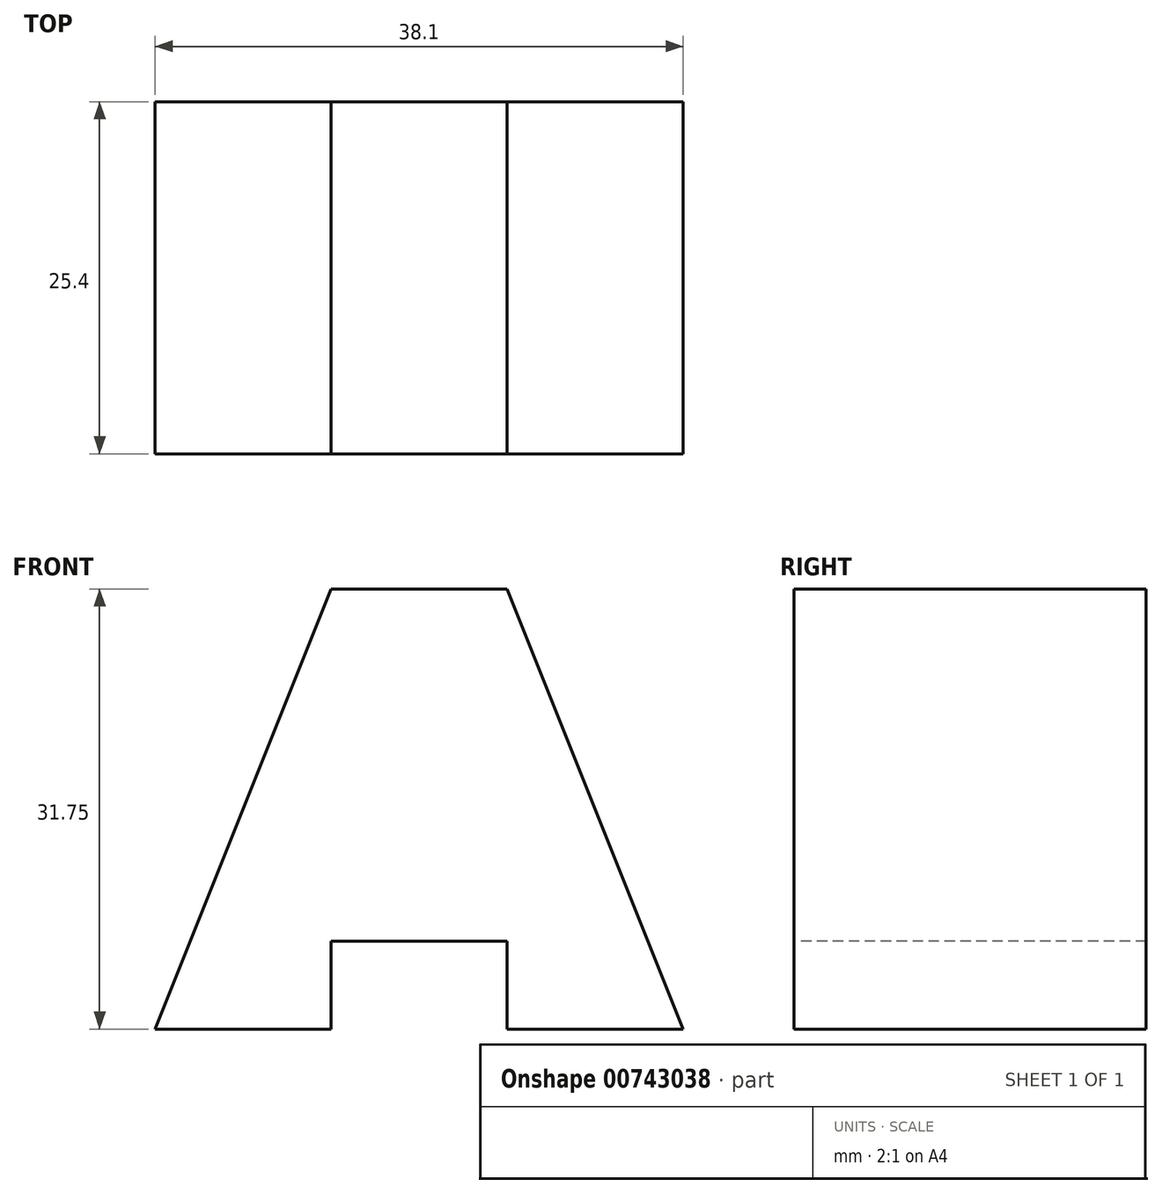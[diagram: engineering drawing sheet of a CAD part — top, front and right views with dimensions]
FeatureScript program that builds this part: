
annotation { "Feature Type Name" : "Feature", "Feature Type Description" : "" }
export const myFeature = defineFeature(function(context is Context, id is Id, definition is map)
    precondition{}
    {
        {
            var Q0;
            Q0=qCreatedBy(makeId("Front.planeOp"),FACE);
            var sketch = newSketch(context, id + "F0", { "sketchPlane" : qUnion([Q0])});
            skLineSegment(sketch, "E0", {"start": v(0, 0) * mm, "end": v(38.1, 0) * mm});
            skLineSegment(sketch, "E1", {"start": v(38.1, 0) * mm, "end": v(38.1, 31.75) * mm});
            skLineSegment(sketch, "E2", {"start": v(38.1, 31.75) * mm, "end": v(0, 31.75) * mm});
            skLineSegment(sketch, "E3", {"start": v(0, 31.75) * mm, "end": v(0, 0) * mm});
            skSolve(sketch);
        }
        {
            var Q0;
            Q0=makeQuery(id+"F0.imprint","IMPRINT",FACE,{"disambiguationData":[TD([[makeQuery(id+"F0.imprint","IMPRINT",EDGE,{"derivedFrom":sQuery(id+"F0.wireOp",EDGE,"E0")}),1.0]])]});
            extrude(context, id + "F1", {"entities" : qUnion([Q0]), "depth" : 25.4 * mm, "offsetDistance" : 25.4 * mm});
        }
        {
            var Q0;
            Q0=makeQuery(id+"F1.opExtrude","CAP_FACE",FACE,{"disambiguationData":[OSD([sQuery(id+"F0.wireOp",EDGE,"E0"),sQuery(id+"F0.wireOp",EDGE,"E1"),sQuery(id+"F0.wireOp",EDGE,"E2"),sQuery(id+"F0.wireOp",EDGE,"E3")])],"isStart":false});
            var sketch = newSketch(context, id + "F2", { "sketchPlane" : qUnion([Q0])});
            skLineSegment(sketch, "E4", {"start": v(12.7, 0) * mm, "end": v(12.7, 6.35) * mm});
            skLineSegment(sketch, "E5", {"start": v(12.7, 6.35) * mm, "end": v(25.4, 6.35) * mm});
            skLineSegment(sketch, "E6", {"start": v(25.4, 6.35) * mm, "end": v(25.4, 0) * mm});
            skLineSegment(sketch, "E7", {"start": v(25.4, 0) * mm, "end": v(12.7, 0) * mm});
            skSolve(sketch);
        }
        {
            var Q0;
            Q0=makeQuery(id+"F2.imprint","IMPRINT",FACE,{"disambiguationData":[TD([[makeQuery(id+"F2.imprint","IMPRINT",EDGE,{"derivedFrom":sQuery(id+"F2.wireOp",EDGE,"E4")}),-1.0]])]});
            extrude(context, id + "F3", {"entities" : qUnion([Q0]), "operationType" : NewBodyOperationType.REMOVE, "oppositeDirection" : true, "depth" : 25.4 * mm, "offsetDistance" : 25.4 * mm});
        }
        {
            var Q0;
            Q0=makeQuery(id+"F1.opExtrude","CAP_FACE",FACE,{"disambiguationData":[OSD([sQuery(id+"F0.wireOp",EDGE,"E0"),sQuery(id+"F0.wireOp",EDGE,"E1"),sQuery(id+"F0.wireOp",EDGE,"E2"),sQuery(id+"F0.wireOp",EDGE,"E3")])],"isStart":false});
            var sketch = newSketch(context, id + "F4", { "sketchPlane" : qUnion([Q0])});
            skLineSegment(sketch, "E8", {"start": v(38.1, 0) * mm, "end": v(25.4, 31.75) * mm});
            skLineSegment(sketch, "E9", {"start": v(0, 0) * mm, "end": v(12.7, 31.75) * mm});
            skSolve(sketch);
        }
        {
            var Q0;
            {var subQ0=sQuery(id+"F4.wireOp",EDGE,"E9");Q0=makeQuery(id+"F4.imprint","IMPRINT",FACE,{"disambiguationData":[TD([[makeQuery(id+"F4.imprint","IMPRINT",EDGE,{"derivedFrom":subQ0}),1.0]])]});}
            var Q1;
            {var subQ0=sQuery(id+"F4.wireOp",EDGE,"E8");Q1=makeQuery(id+"F4.imprint","IMPRINT",FACE,{"disambiguationData":[TD([[makeQuery(id+"F4.imprint","IMPRINT",EDGE,{"derivedFrom":subQ0}),-1.0]])]});}
            extrude(context, id + "F5", {"entities" : qUnion([Q0, Q1]), "operationType" : NewBodyOperationType.REMOVE, "oppositeDirection" : true, "depth" : 25.4 * mm, "offsetDistance" : 25.4 * mm});
        }
    });
